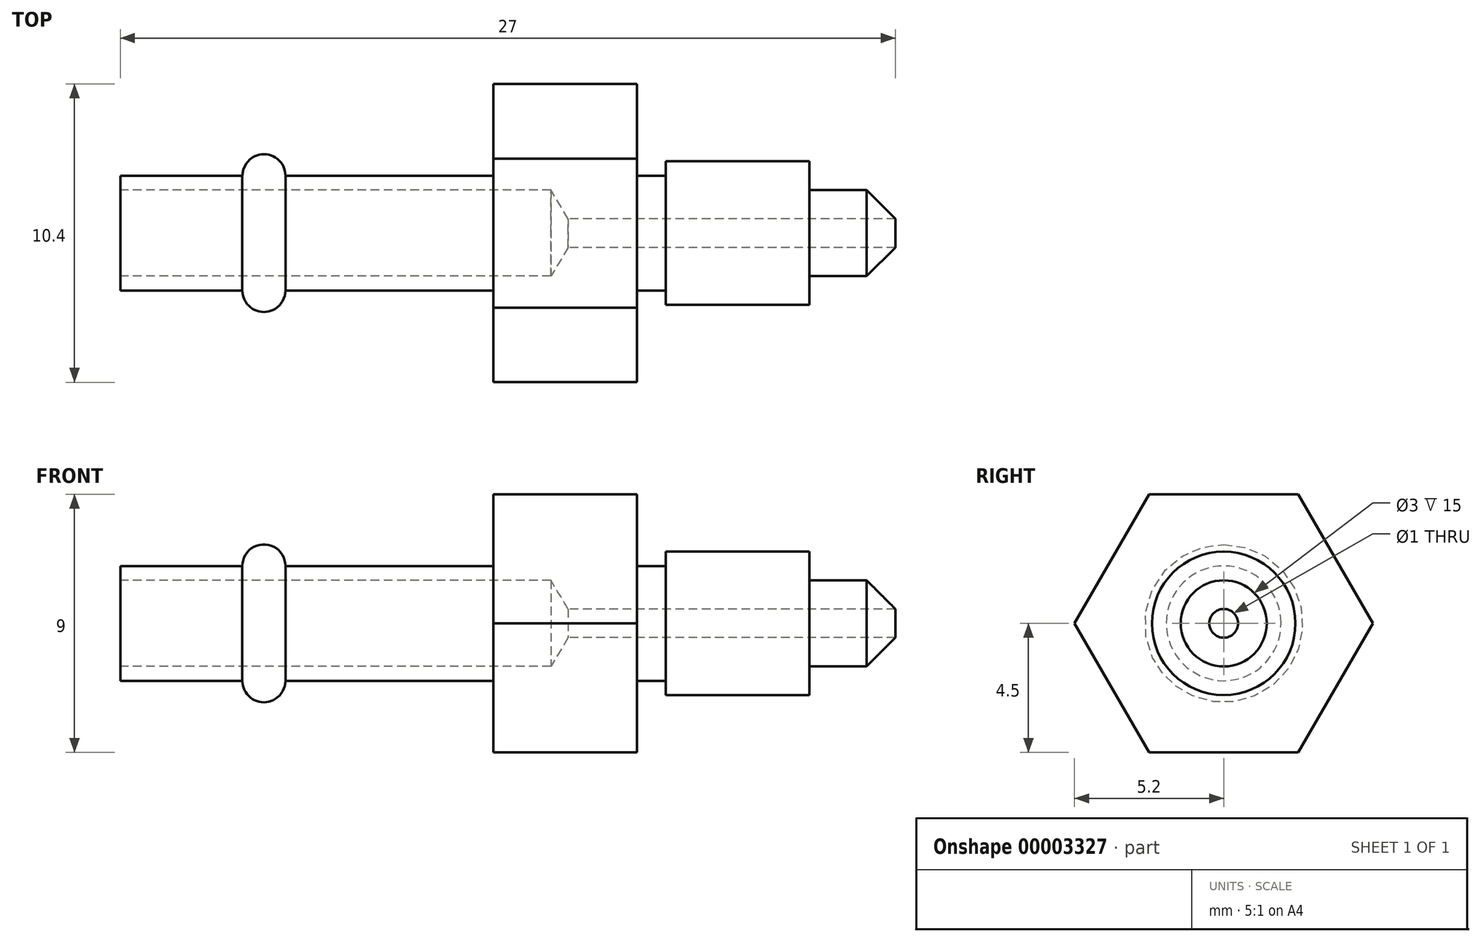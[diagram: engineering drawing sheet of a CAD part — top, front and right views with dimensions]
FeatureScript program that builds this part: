
annotation { "Feature Type Name" : "Feature", "Feature Type Description" : "" }
export const myFeature = defineFeature(function(context is Context, id is Id, definition is map)
    precondition{}
    {
        {
            var Q0;
            Q0=qCreatedBy(makeId("Front.planeOp"),FACE);
            var sketch = newSketch(context, id + "F0", { "sketchPlane" : qUnion([Q0])});
            skLineSegment(sketch, "E0", {"start": v(0, 0) * mm, "end": v(27, 0) * mm});
            skLineSegment(sketch, "E1", {"start": v(0, 1.5) * mm, "end": v(0, 2) * mm});
            skLineSegment(sketch, "E2", {"start": v(0, 2) * mm, "end": v(4.25, 2) * mm});
            skLineSegment(sketch, "E3", {"start": v(19, 2) * mm, "end": v(19, 2.5) * mm});
            skLineSegment(sketch, "E4", {"start": v(19, 2.5) * mm, "end": v(24, 2.5) * mm});
            skLineSegment(sketch, "E5", {"start": v(24, 2.5) * mm, "end": v(24, 1.5) * mm});
            skLineSegment(sketch, "E6", {"start": v(24, 1.5) * mm, "end": v(26, 1.5) * mm});
            skLineSegment(sketch, "E7", {"start": v(26, 1.5) * mm, "end": v(27, 0.5) * mm});
            skLineSegment(sketch, "E8", {"start": v(27, 0.5) * mm, "end": v(15.6, 0.5) * mm});
            skLineSegment(sketch, "E9", {"start": v(15.6, 0.5) * mm, "end": v(15, 1.5) * mm});
            skLineSegment(sketch, "E10", {"start": v(15, 1.5) * mm, "end": v(0, 1.5) * mm});
            skLineSegment(sketch, "E11.0.MirrorCS", {"start": v(27, -0.5) * mm, "end": v(15.6, -0.5) * mm});
            skLineSegment(sketch, "E12.0.MirrorCS", {"start": v(26, -1.5) * mm, "end": v(27, -0.5) * mm});
            skLineSegment(sketch, "E13.0.MirrorCS", {"start": v(24, -1.5) * mm, "end": v(26, -1.5) * mm});
            skLineSegment(sketch, "E14.0.MirrorCS", {"start": v(24, -2.5) * mm, "end": v(24, -1.5) * mm});
            skLineSegment(sketch, "E15.0.MirrorCS", {"start": v(19, -2.5) * mm, "end": v(24, -2.5) * mm});
            skLineSegment(sketch, "E16.0.MirrorCS", {"start": v(19, -2) * mm, "end": v(19, -2.5) * mm});
            skLineSegment(sketch, "E17.0.MirrorCS", {"start": v(0, -2) * mm, "end": v(4.25, -2) * mm});
            skLineSegment(sketch, "E18.0.MirrorCS", {"start": v(0, -1.5) * mm, "end": v(0, -2) * mm});
            skLineSegment(sketch, "E19.0.MirrorCS", {"start": v(15, -1.5) * mm, "end": v(0, -1.5) * mm});
            skLineSegment(sketch, "E20.0.MirrorCS", {"start": v(15.6, -0.5) * mm, "end": v(15, -1.5) * mm});
            skArc(sketch, "E21", {"start": v(5.75, 2) * mm, "mid": v(5, 2.75) * mm, "end": v(4.25, 2) * mm});
            skArc(sketch, "E22.0.MirrorC", {"start": v(5.75, -2) * mm, "mid": v(5, -2.75) * mm, "end": v(4.25, -2) * mm});
            skLineSegment(sketch, "E23", {"start": v(18, 2) * mm, "end": v(18, 3.65) * mm});
            skLineSegment(sketch, "E24", {"start": v(18, 3.65) * mm, "end": v(13, 3.65) * mm});
            skLineSegment(sketch, "E25", {"start": v(13, 3.65) * mm, "end": v(13, 2) * mm});
            skLineSegment(sketch, "E26.trimOffspring", {"start": v(5.75, 2) * mm, "end": v(19, 2) * mm});
            skLineSegment(sketch, "E27.trimOffspring", {"start": v(5.75, -2) * mm, "end": v(19, -2) * mm});
            skSolve(sketch);
        }
        {
            var Q0;
            Q0=makeQuery(id+"F0.imprint","IMPRINT",FACE,{"disambiguationData":[TD([[makeQuery(id+"F0.imprint","IMPRINT",EDGE,{"derivedFrom":sQuery(id+"F0.wireOp",EDGE,"E1")}),-1.0]])]});
            var Q1;
            {var subQ2=sQuery(id+"F0.wireOp",EDGE,"E23");Q1=makeQuery(id+"F0.imprint","IMPRINT",FACE,{"disambiguationData":[TD([[makeQuery(id+"F0.imprint","IMPRINT",EDGE,{"derivedFrom":subQ2}),1.0]])]});}
            var Q2;
            Q2=sQuery(id+"F0.wireOp",EDGE,"E0");
            revolve(context, id + "F1", {"entities" : qUnion([Q0, Q1]), "axis" : qUnion([Q2]), "revolveType" : RevolveType.FULL});
        }
        {
            var Q0;
            Q0=makeQuery(id+"F1.opRevolve","SWEPT_FACE",FACE,{"disambiguationData":[OSD([sQuery(id+"F0.wireOp",EDGE,"E25")])]});
            var sketch = newSketch(context, id + "F2", { "sketchPlane" : qUnion([Q0])});
            skCircle(sketch, "E28.cCircle", {"center": v(0, 0) * mm, "radius": 4.5 * mm, "construction": true});
            skLineSegment(sketch, "E28.0", {"start": v(-2.6, 4.5) * mm, "end": v(2.6, 4.5) * mm});
            skLineSegment(sketch, "E28.1", {"start": v(2.6, 4.5) * mm, "end": v(5.2, 0) * mm});
            skLineSegment(sketch, "E28.2", {"start": v(5.2, 0) * mm, "end": v(2.6, -4.5) * mm});
            skLineSegment(sketch, "E28.3", {"start": v(2.6, -4.5) * mm, "end": v(-2.6, -4.5) * mm});
            skLineSegment(sketch, "E28.4", {"start": v(-2.6, -4.5) * mm, "end": v(-5.2, 0) * mm});
            skLineSegment(sketch, "E28.5", {"start": v(-5.2, 0) * mm, "end": v(-2.6, 4.5) * mm});
            skPoint(sketch, "E28.0.midPoint", {"position": v(0, 4.5) * mm});
            skSolve(sketch);
        }
        {
            var Q0;
            Q0=makeQuery(id+"F2.imprint","IMPRINT",FACE,{"disambiguationData":[TD([[makeQuery(id+"F2.imprint","IMPRINT",EDGE,{"derivedFrom":sQuery(id+"F2.wireOp",EDGE,"E28.0")}),-1.0]])]});
            var Q1;
            Q1=makeQuery(id+"F1.opRevolve","SWEPT_FACE",FACE,{"disambiguationData":[OSD([sQuery(id+"F0.wireOp",EDGE,"E23")])]});
            extrude(context, id + "F3", {"entities" : qUnion([Q0]), "operationType" : NewBodyOperationType.ADD, "endBound" : BoundingType.UP_TO_SURFACE, "oppositeDirection" : true, "endBoundEntityFace" : qUnion([Q1]), "depth" : 25 * mm});
        }
    });
